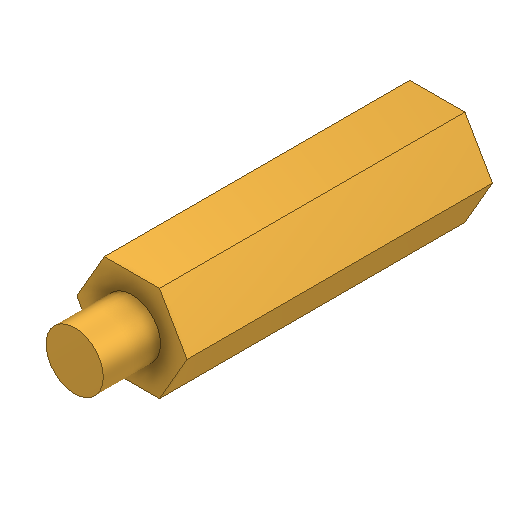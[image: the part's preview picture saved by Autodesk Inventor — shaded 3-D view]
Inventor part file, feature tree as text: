
AUTODESK INVENTOR PART (.ipt)
format: ipt  version: 2025.2 (Build 292293000, 293)  size: 115,200 bytes
history: native  units: mm
features: extrude x2, sketch x2
ambient origin geometry x8: Origin, YZ Plane, XZ Plane, XY Plane, X Axis, Y Axis, Z Axis, Center Point
bodies: Solid1 (feature_tree)
feature tree (4):
  extrude  "Extrusion1"  Depth=3.0mm
  extrude  "Extrusion2"  Depth=3.0mm TaperAngle=0.0deg
  sketch  "Sketch1"  dims[d0=5.0mm d1=3.0mm]
  sketch  "Sketch2"  dims[d2=16.0mm d3=0.0mm d4=3.0mm d5=0.0mm]
